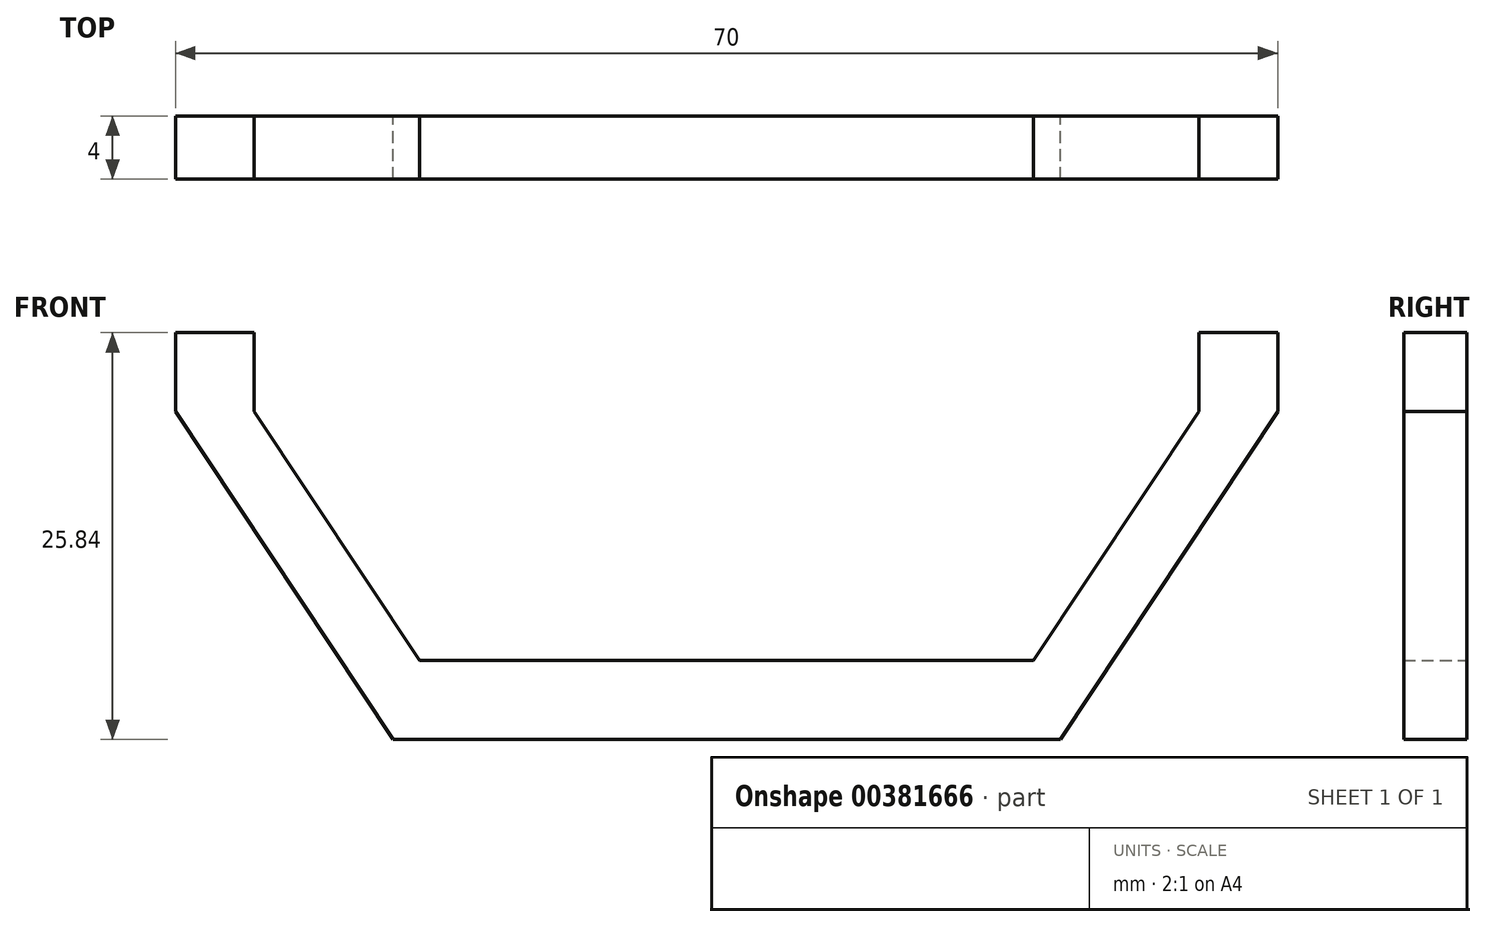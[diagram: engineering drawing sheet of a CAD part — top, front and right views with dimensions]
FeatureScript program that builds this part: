
annotation { "Feature Type Name" : "Feature", "Feature Type Description" : "" }
export const myFeature = defineFeature(function(context is Context, id is Id, definition is map)
    precondition{}
    {
        {
            var Q0;
            Q0=qCreatedBy(makeId("Front.planeOp"),FACE);
            var sketch = newSketch(context, id + "F0", { "sketchPlane" : qUnion([Q0])});
            skLineSegment(sketch, "E0", {"start": v(0, 0) * mm, "end": v(30, 0) * mm, "construction": true});
            skLineSegment(sketch, "E1", {"start": v(30, 0) * mm, "end": v(35, 0) * mm});
            skLineSegment(sketch, "E2", {"start": v(35, 0) * mm, "end": v(35, -5) * mm});
            skLineSegment(sketch, "E3", {"start": v(35, -5) * mm, "end": v(21.19, -25.84) * mm});
            skLineSegment(sketch, "E4", {"start": v(21.19, -25.84) * mm, "end": v(0, -25.84) * mm});
            skLineSegment(sketch, "E5", {"start": v(30, 0) * mm, "end": v(30, -5) * mm});
            skLineSegment(sketch, "E6", {"start": v(0, -25.84) * mm, "end": v(0, -20.84) * mm});
            skLineSegment(sketch, "E7", {"start": v(0, -20.84) * mm, "end": v(19.5, -20.84) * mm});
            skLineSegment(sketch, "E8", {"start": v(30, -5) * mm, "end": v(19.5, -20.84) * mm});
            skPoint(sketch, "E9.orphan", {"position": v(21.19, -20.84) * mm});
            skLineSegment(sketch, "E10.MirrorCS", {"start": v(-30, 0) * mm, "end": v(-35, 0) * mm});
            skLineSegment(sketch, "E11.MirrorCS", {"start": v(-30, 0) * mm, "end": v(-30, -5) * mm});
            skLineSegment(sketch, "E12.MirrorCS", {"start": v(-35, 0) * mm, "end": v(-35, -5) * mm});
            skLineSegment(sketch, "E13.MirrorCS", {"start": v(0, 0) * mm, "end": v(-30, 0) * mm, "construction": true});
            skLineSegment(sketch, "E14.MirrorCS", {"start": v(-30, -5) * mm, "end": v(-19.5, -20.84) * mm});
            skLineSegment(sketch, "E15.MirrorCS", {"start": v(-35, -5) * mm, "end": v(-21.19, -25.84) * mm});
            skPoint(sketch, "E16.MirrorP", {"position": v(-21.19, -20.84) * mm});
            skLineSegment(sketch, "E17.MirrorCS", {"start": v(-21.19, -25.84) * mm, "end": v(0, -25.84) * mm});
            skLineSegment(sketch, "E18.MirrorCS", {"start": v(0, -20.84) * mm, "end": v(-19.5, -20.84) * mm});
            skSolve(sketch);
        }
        {
            var Q0;
            Q0 = qSketchRegion(id + "F0", true);
            extrude(context, id + "F1", {"entities" : qUnion([Q0]), "depth" : 4 * mm});
        }
    });
